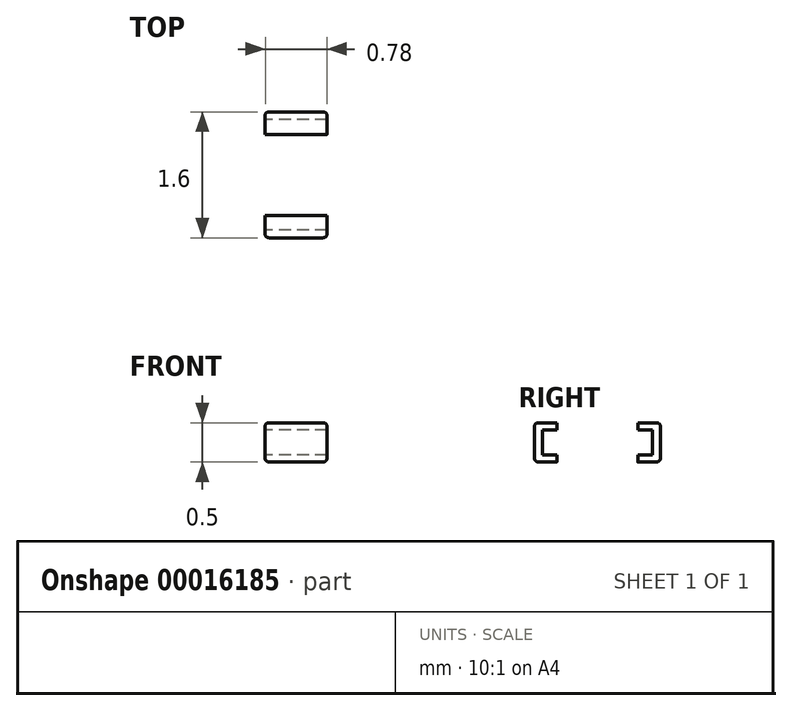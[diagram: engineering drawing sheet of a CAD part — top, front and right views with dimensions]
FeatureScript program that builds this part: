
annotation { "Feature Type Name" : "Feature", "Feature Type Description" : "" }
export const myFeature = defineFeature(function(context is Context, id is Id, definition is map)
    precondition{}
    {
        {
            var Q0;
            Q0=qCreatedBy(makeId("Right.planeOp"),FACE);
            var sketch = newSketch(context, id + "F0", { "sketchPlane" : qUnion([Q0])});
            skLineSegment(sketch, "E0.rect.bottom", {"start": v(0.8, 0.25) * mm, "end": v(-0.8, 0.25) * mm});
            skLineSegment(sketch, "E0.rect.top", {"start": v(0.8, -0.25) * mm, "end": v(-0.8, -0.25) * mm});
            skLineSegment(sketch, "E0.rect.left", {"start": v(0.8, 0.25) * mm, "end": v(0.8, -0.25) * mm});
            skLineSegment(sketch, "E0.rect.right", {"start": v(-0.8, 0.25) * mm, "end": v(-0.8, -0.25) * mm});
            skPoint(sketch, "E0.rect.middle", {"position": v(0, 0) * mm});
            skLineSegment(sketch, "E1", {"start": v(-0.51, 0.25) * mm, "end": v(-0.51, 0.16) * mm});
            skLineSegment(sketch, "E2", {"start": v(-0.51, 0.16) * mm, "end": v(-0.7, 0.16) * mm});
            skLineSegment(sketch, "E3", {"start": v(-0.7, 0.16) * mm, "end": v(-0.7, -0.16) * mm});
            skLineSegment(sketch, "E4", {"start": v(-0.7, -0.16) * mm, "end": v(-0.51, -0.16) * mm});
            skLineSegment(sketch, "E5", {"start": v(-0.51, -0.16) * mm, "end": v(-0.51, -0.25) * mm});
            skLineSegment(sketch, "E6.MirrorCS", {"start": v(0.51, 0.25) * mm, "end": v(0.51, 0.16) * mm});
            skLineSegment(sketch, "E7.MirrorCS", {"start": v(0.51, 0.16) * mm, "end": v(0.7, 0.16) * mm});
            skLineSegment(sketch, "E8.MirrorCS", {"start": v(0.7, 0.16) * mm, "end": v(0.7, -0.16) * mm});
            skLineSegment(sketch, "E9.MirrorCS", {"start": v(0.7, -0.16) * mm, "end": v(0.51, -0.16) * mm});
            skLineSegment(sketch, "E10.MirrorCS", {"start": v(0.51, -0.16) * mm, "end": v(0.51, -0.25) * mm});
            skLineSegment(sketch, "E11.bottom", {"start": v(0.51, 0.24) * mm, "end": v(-0.51, 0.24) * mm});
            skLineSegment(sketch, "E11.top", {"start": v(0.51, -0.24) * mm, "end": v(-0.51, -0.24) * mm});
            skLineSegment(sketch, "E11.left", {"start": v(0.51, 0.24) * mm, "end": v(0.51, -0.24) * mm});
            skLineSegment(sketch, "E11.right", {"start": v(-0.51, 0.24) * mm, "end": v(-0.51, -0.24) * mm});
            skSolve(sketch);
        }
        {
            var Q0;
            {var subQ5=sQuery(id+"F0.wireOp",EDGE,"E0.rect.right");Q0=makeQuery(id+"F0.imprint","IMPRINT",FACE,{"disambiguationData":[TD([[makeQuery(id+"F0.imprint","IMPRINT",EDGE,{"derivedFrom":subQ5}),1.0]])]});}
            var Q1;
            {var subQ5=sQuery(id+"F0.wireOp",EDGE,"E0.rect.left");Q1=makeQuery(id+"F0.imprint","IMPRINT",FACE,{"disambiguationData":[TD([[makeQuery(id+"F0.imprint","IMPRINT",EDGE,{"derivedFrom":subQ5}),-1.0]])]});}
            extrude(context, id + "F1", {"entities" : qUnion([Q0, Q1]), "endBound" : BoundingType.SYMMETRIC, "depth" : 0.79 * mm});
        }
        {
            var Q0;
            {var subQ0=sQuery(id+"F0.wireOp",EDGE,"E0.rect.bottom");Q0=makeQuery(id+"F1.opExtrude","CAP_EDGE",EDGE,{"disambiguationData":[OSD([subQ0]),TDD([makeQuery(id+"F0.imprint","IMPRINT",EDGE,{"disambiguationData":[TD([[makeQuery(id+"F0.imprint","INTERSECT",VERTEX,{"derivedFrom":[subQ0,sQuery(id+"F0.wireOp",EDGE,"E0.rect.right")]}),1.0]])],"derivedFrom":subQ0})])],"isStart":true});}
            var Q1;
            {var subQ0=sQuery(id+"F0.wireOp",EDGE,"E0.rect.bottom");Q1=makeQuery(id+"F1.opExtrude","CAP_EDGE",EDGE,{"disambiguationData":[OSD([subQ0]),TDD([makeQuery(id+"F0.imprint","IMPRINT",EDGE,{"disambiguationData":[TD([[makeQuery(id+"F0.imprint","INTERSECT",VERTEX,{"derivedFrom":[subQ0,sQuery(id+"F0.wireOp",EDGE,"E0.rect.right")]}),1.0]])],"derivedFrom":subQ0})])],"isStart":false});}
            var Q2;
            Q2=makeQuery(id+"F1.opExtrude","SWEPT_EDGE",EDGE,{"disambiguationData":[OSD([sQuery(id+"F0.wireOp",EDGE,"E0.rect.bottom"),sQuery(id+"F0.wireOp",EDGE,"E0.rect.right")])]});
            var Q3;
            {var subQ0=sQuery(id+"F0.wireOp",EDGE,"E0.rect.bottom");Q3=makeQuery(id+"F1.opExtrude","CAP_EDGE",EDGE,{"disambiguationData":[OSD([subQ0]),TDD([makeQuery(id+"F0.imprint","IMPRINT",EDGE,{"disambiguationData":[TD([[makeQuery(id+"F0.imprint","INTERSECT",VERTEX,{"derivedFrom":[subQ0,sQuery(id+"F0.wireOp",EDGE,"E0.rect.left")]}),-1.0]])],"derivedFrom":subQ0})])],"isStart":false});}
            var Q4;
            Q4=makeQuery(id+"F1.opExtrude","SWEPT_EDGE",EDGE,{"disambiguationData":[OSD([sQuery(id+"F0.wireOp",EDGE,"E0.rect.bottom"),sQuery(id+"F0.wireOp",EDGE,"E0.rect.left")])]});
            var Q5;
            {var subQ0=sQuery(id+"F0.wireOp",EDGE,"E0.rect.bottom");Q5=makeQuery(id+"F1.opExtrude","CAP_EDGE",EDGE,{"disambiguationData":[OSD([subQ0]),TDD([makeQuery(id+"F0.imprint","IMPRINT",EDGE,{"disambiguationData":[TD([[makeQuery(id+"F0.imprint","INTERSECT",VERTEX,{"derivedFrom":[subQ0,sQuery(id+"F0.wireOp",EDGE,"E0.rect.left")]}),-1.0]])],"derivedFrom":subQ0})])],"isStart":true});}
            var Q6;
            Q6=makeQuery(id+"F1.opExtrude","CAP_EDGE",EDGE,{"disambiguationData":[OSD([sQuery(id+"F0.wireOp",EDGE,"E0.rect.right")])],"isStart":false});
            var Q7;
            {var subQ0=sQuery(id+"F0.wireOp",EDGE,"E0.rect.top");Q7=makeQuery(id+"F1.opExtrude","CAP_EDGE",EDGE,{"disambiguationData":[OSD([subQ0]),TDD([makeQuery(id+"F0.imprint","IMPRINT",EDGE,{"disambiguationData":[TD([[makeQuery(id+"F0.imprint","INTERSECT",VERTEX,{"derivedFrom":[subQ0,sQuery(id+"F0.wireOp",EDGE,"E0.rect.right")]}),1.0]])],"derivedFrom":subQ0})])],"isStart":false});}
            var Q8;
            Q8=makeQuery(id+"F1.opExtrude","SWEPT_EDGE",EDGE,{"disambiguationData":[OSD([sQuery(id+"F0.wireOp",EDGE,"E0.rect.top"),sQuery(id+"F0.wireOp",EDGE,"E0.rect.right")])]});
            var Q9;
            Q9=makeQuery(id+"F1.opExtrude","CAP_EDGE",EDGE,{"disambiguationData":[OSD([sQuery(id+"F0.wireOp",EDGE,"E0.rect.right")])],"isStart":true});
            var Q10;
            {var subQ0=sQuery(id+"F0.wireOp",EDGE,"E0.rect.top");Q10=makeQuery(id+"F1.opExtrude","CAP_EDGE",EDGE,{"disambiguationData":[OSD([subQ0]),TDD([makeQuery(id+"F0.imprint","IMPRINT",EDGE,{"disambiguationData":[TD([[makeQuery(id+"F0.imprint","INTERSECT",VERTEX,{"derivedFrom":[subQ0,sQuery(id+"F0.wireOp",EDGE,"E0.rect.left")]}),-1.0]])],"derivedFrom":subQ0})])],"isStart":false});}
            var Q11;
            Q11=makeQuery(id+"F1.opExtrude","CAP_EDGE",EDGE,{"disambiguationData":[OSD([sQuery(id+"F0.wireOp",EDGE,"E0.rect.left")])],"isStart":false});
            var Q12;
            Q12=makeQuery(id+"F1.opExtrude","SWEPT_EDGE",EDGE,{"disambiguationData":[OSD([sQuery(id+"F0.wireOp",EDGE,"E0.rect.top"),sQuery(id+"F0.wireOp",EDGE,"E0.rect.left")])]});
            var Q13;
            {var subQ0=sQuery(id+"F0.wireOp",EDGE,"E0.rect.top");Q13=makeQuery(id+"F1.opExtrude","CAP_EDGE",EDGE,{"disambiguationData":[OSD([subQ0]),TDD([makeQuery(id+"F0.imprint","IMPRINT",EDGE,{"disambiguationData":[TD([[makeQuery(id+"F0.imprint","INTERSECT",VERTEX,{"derivedFrom":[subQ0,sQuery(id+"F0.wireOp",EDGE,"E0.rect.left")]}),-1.0]])],"derivedFrom":subQ0})])],"isStart":true});}
            var Q14;
            Q14=makeQuery(id+"F1.opExtrude","CAP_EDGE",EDGE,{"disambiguationData":[OSD([sQuery(id+"F0.wireOp",EDGE,"E0.rect.left")])],"isStart":true});
            var Q15;
            {var subQ0=sQuery(id+"F0.wireOp",EDGE,"E0.rect.top");Q15=makeQuery(id+"F1.opExtrude","CAP_EDGE",EDGE,{"disambiguationData":[OSD([subQ0]),TDD([makeQuery(id+"F0.imprint","IMPRINT",EDGE,{"disambiguationData":[TD([[makeQuery(id+"F0.imprint","INTERSECT",VERTEX,{"derivedFrom":[subQ0,sQuery(id+"F0.wireOp",EDGE,"E0.rect.right")]}),1.0]])],"derivedFrom":subQ0})])],"isStart":true});}
            fillet(context, id + "F2", {"entities" : qUnion([Q0, Q1, Q2, Q3, Q4, Q5, Q6, Q7, Q8, Q9, Q10, Q11, Q12, Q13, Q14, Q15]), "radius" : 0.05 * mm, "allowEdgeOverflow" : false});
        }
    });
